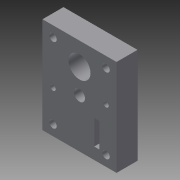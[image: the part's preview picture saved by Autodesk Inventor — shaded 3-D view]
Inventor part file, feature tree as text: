
AUTODESK INVENTOR PART (.ipt)
format: ipt  version: 2015 (Build 190159000, 159)  size: 125,952 bytes
history: native  units: mm
features: extrude x1, sketch x1
ambient origin geometry x8: Origin, YZ Plane, XZ Plane, XY Plane, X Axis, Y Axis, Z Axis, Center Point
bodies: Solid1 (feature_tree)
feature tree (2):
  extrude  "Extrusion1"  Depth=23.5mm
  sketch  "Sketch1"  dims[d0=21.0mm d1=23.5mm d2=10.5mm d3=11.75mm d5=23.5mm d6=5.0mm d7=23.5mm d9=70.5mm d40=21.625mm d41=70.5mm d42=91.5mm d43=10.0mm d44=10.0mm d45=7.0mm d46=10.0mm d47=10.0mm d48=90.0deg d50=7.0mm d51=10.0mm d52=10.0mm d53=7.0mm d54=10.0mm d55=10.0mm d56=7.0mm d60=30.0mm d61=30.0mm d62=5.0mm d63=5.0mm d64=14.0mm d65=20.0mm d66=0.0mm]
